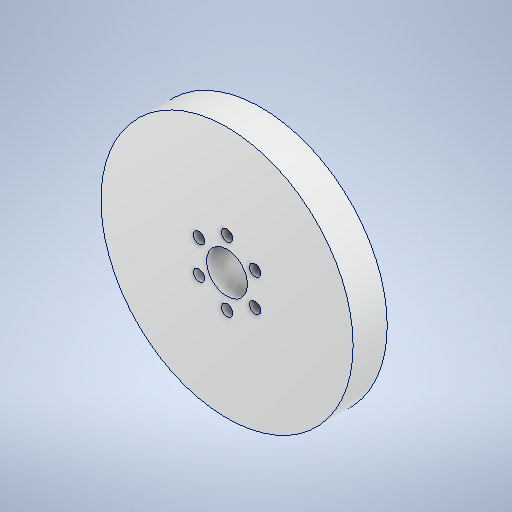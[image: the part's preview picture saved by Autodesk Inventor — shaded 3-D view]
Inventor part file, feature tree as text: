
AUTODESK INVENTOR PART (.ipt)
format: ipt  version: 2025.2 (Build 292293000, 293)  size: 270,336 bytes
history: native  units: in
note: dims shown in document units (in); Inventor stores cm internally (conversion verified against a paired STEP export)
features: sketch x5, extrude x4
ambient origin geometry x8: Origin, YZ Plane, XZ Plane, XY Plane, X Axis, Y Axis, Z Axis, Center Point
bodies: Solid1 (feature_tree)
feature tree (9):
  extrude  "Extrusion1"  Depth=0.3937in TaperAngle=0.0deg
  extrude  "Extrusion3"  Depth=1.3386in
  extrude  "Extrusion4"  Depth=0.2362in
  extrude  "Extrusion6"  Depth=0.2756in
  sketch  "Sketch1"  dims[d0=2.9134in d1=0.3937in d2=0.0in]
  sketch  "Sketch4"  dims[d7=0.2362in d8=0.0in d9=1.1811in]
  sketch  "Sketch6"  dims[d10=0.2756in d11=0.0in d16=0.748in]
  sketch  "Sketch8"  dims[d17=0.1299in d18=2.3622in d20=360.0deg d22=0.0in d23=0.0in d24=0.4724in]
  sketch  "Sketch Circular Pattern1"  dims[d5=0.315in d6=1.3386in]
